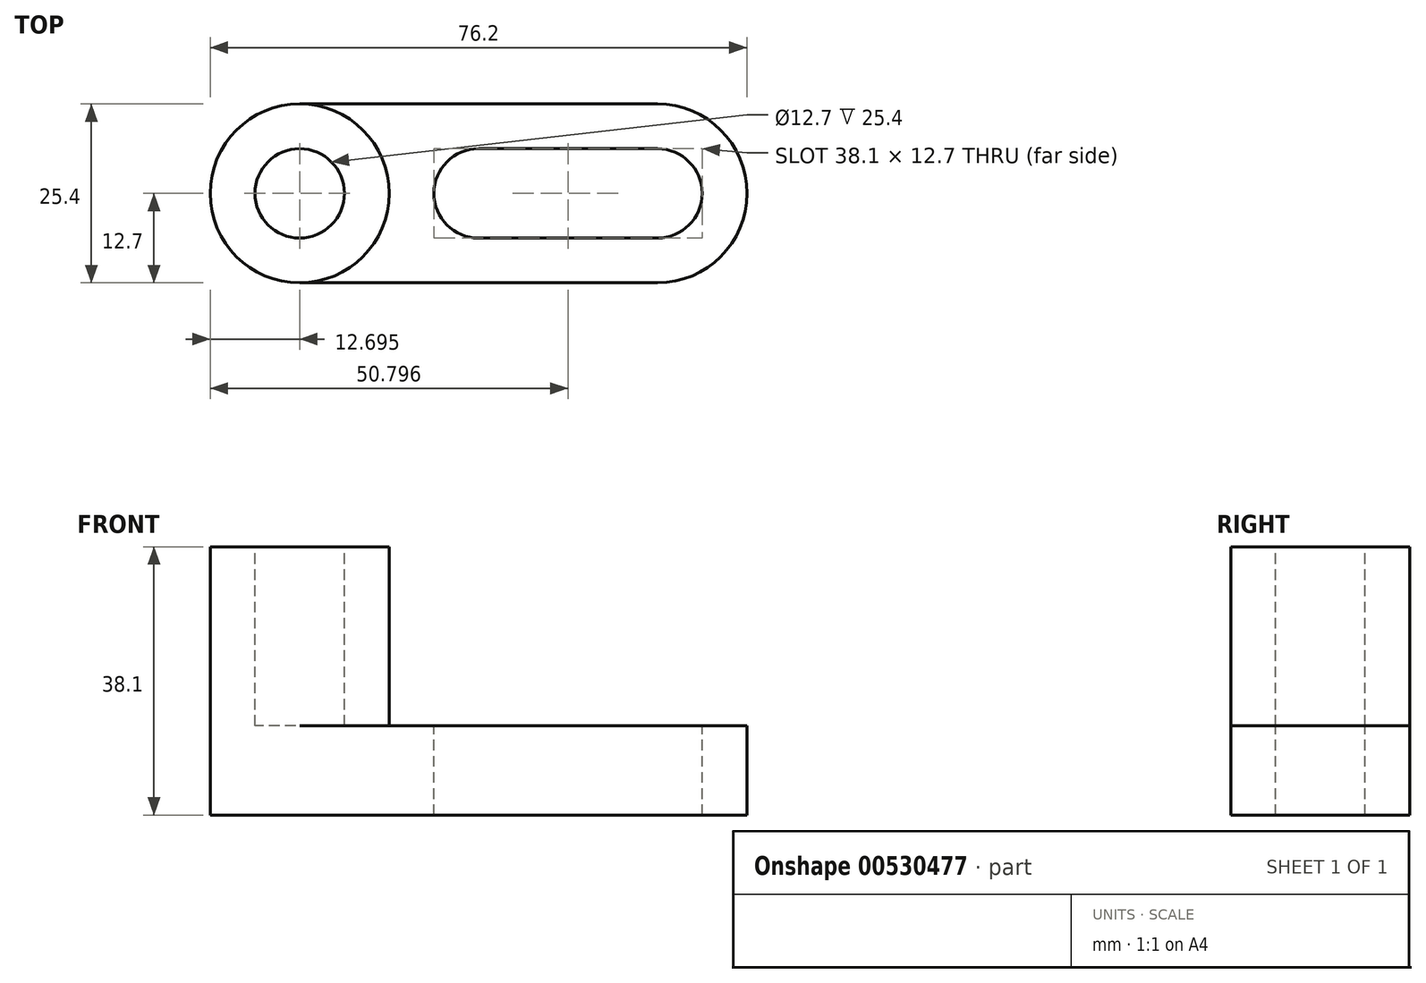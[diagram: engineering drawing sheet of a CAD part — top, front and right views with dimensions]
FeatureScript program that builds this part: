
annotation { "Feature Type Name" : "Feature", "Feature Type Description" : "" }
export const myFeature = defineFeature(function(context is Context, id is Id, definition is map)
    precondition{}
    {
        {
            var Q0;
            Q0=qCreatedBy(makeId("Front.planeOp"),FACE);
            var sketch = newSketch(context, id + "F0", { "sketchPlane" : qUnion([Q0])});
            skLineSegment(sketch, "E0", {"start": v(-91.03, 0) * mm, "end": v(-14.83, 0) * mm});
            skLineSegment(sketch, "E1", {"start": v(-14.83, 0) * mm, "end": v(-14.83, 12.7) * mm});
            skLineSegment(sketch, "E2", {"start": v(-14.83, 12.7) * mm, "end": v(-65.63, 12.7) * mm});
            skLineSegment(sketch, "E3", {"start": v(-65.63, 12.7) * mm, "end": v(-65.63, 38.1) * mm});
            skLineSegment(sketch, "E4", {"start": v(-65.63, 38.1) * mm, "end": v(-91.03, 38.1) * mm});
            skLineSegment(sketch, "E5", {"start": v(-91.03, 38.1) * mm, "end": v(-91.03, 0) * mm});
            skSolve(sketch);
        }
        {
            var Q0;
            Q0=makeQuery(id+"F0.imprint","IMPRINT",FACE,{"disambiguationData":[TD([[makeQuery(id+"F0.imprint","IMPRINT",EDGE,{"derivedFrom":sQuery(id+"F0.wireOp",EDGE,"E0")}),1.0]])]});
            extrude(context, id + "F1", {"entities" : qUnion([Q0]), "depth" : 25.4 * mm, "offsetDistance" : 25.4 * mm});
        }
        {
            var Q0;
            Q0=makeQuery(id+"F1.opExtrude","SWEPT_FACE",FACE,{"disambiguationData":[OSD([sQuery(id+"F0.wireOp",EDGE,"E4")])]});
            var sketch = newSketch(context, id + "F2", { "sketchPlane" : qUnion([Q0])});
            skCircle(sketch, "E6", {"center": v(-78.33, -12.7) * mm, "radius": 12.7 * mm});
            skPoint(sketch, "E6.centerSnap0", {"position": v(-65.63, -12.7) * mm});
            skCircle(sketch, "E7", {"center": v(-78.33, -12.7) * mm, "radius": 6.35 * mm});
            skSolve(sketch);
        }
        {
            var Q0;
            {var subQ0=sQuery(id+"F2.wireOp",EDGE,"E6");var subQ1=sQuery(id+"F0.wireOp",EDGE,"E4");var subQ2=makeQuery(id+"F1.opExtrude","CAP_EDGE",EDGE,{"disambiguationData":[OSD([subQ1])],"isStart":true});var subQ3=makeQuery(id+"F2.imprint","INTERSECT",VERTEX,{"derivedFrom":[subQ2,subQ0]});Q0=makeQuery(id+"F2.imprint","IMPRINT",FACE,{"disambiguationData":[TD([[makeQuery(id+"F2.imprint","IMPRINT",EDGE,{"disambiguationData":[TD([[subQ3,1.0]])],"derivedFrom":subQ0}),-1.0]])]});}
            var Q1;
            Q1=makeQuery(id+"F2.imprint","IMPRINT",FACE,{"disambiguationData":[TD([[makeQuery(id+"F2.imprint","IMPRINT",EDGE,{"derivedFrom":sQuery(id+"F2.wireOp",EDGE,"E7")}),1.0]])]});
            var Q2;
            {var subQ0=sQuery(id+"F2.wireOp",EDGE,"E6");var subQ1=sQuery(id+"F0.wireOp",EDGE,"E4");var subQ4=makeQuery(id+"F1.opExtrude","CAP_EDGE",EDGE,{"disambiguationData":[OSD([subQ1])],"isStart":false});var subQ5=makeQuery(id+"F2.imprint","INTERSECT",VERTEX,{"derivedFrom":[subQ4,subQ0]});Q2=makeQuery(id+"F2.imprint","IMPRINT",FACE,{"disambiguationData":[TD([[makeQuery(id+"F2.imprint","IMPRINT",EDGE,{"disambiguationData":[TD([[subQ5,-1.0]])],"derivedFrom":subQ0}),-1.0]])]});}
            var Q3;
            {var subQ0=sQuery(id+"F2.wireOp",EDGE,"E6");var subQ1=sQuery(id+"F0.wireOp",EDGE,"E4");var subQ4=makeQuery(id+"F1.opExtrude","CAP_EDGE",EDGE,{"disambiguationData":[OSD([subQ1])],"isStart":false});var subQ5=makeQuery(id+"F2.imprint","INTERSECT",VERTEX,{"derivedFrom":[subQ4,subQ0]});Q3=makeQuery(id+"F2.imprint","IMPRINT",FACE,{"disambiguationData":[TD([[makeQuery(id+"F2.imprint","IMPRINT",EDGE,{"disambiguationData":[TD([[subQ5,1.0]])],"derivedFrom":subQ0}),-1.0]])]});}
            var Q4;
            {var subQ0=sQuery(id+"F2.wireOp",EDGE,"E6");var subQ1=sQuery(id+"F0.wireOp",EDGE,"E4");var subQ2=makeQuery(id+"F1.opExtrude","CAP_EDGE",EDGE,{"disambiguationData":[OSD([subQ1])],"isStart":true});var subQ3=makeQuery(id+"F2.imprint","INTERSECT",VERTEX,{"derivedFrom":[subQ2,subQ0]});Q4=makeQuery(id+"F2.imprint","IMPRINT",FACE,{"disambiguationData":[TD([[makeQuery(id+"F2.imprint","IMPRINT",EDGE,{"disambiguationData":[TD([[subQ3,-1.0]])],"derivedFrom":subQ0}),-1.0]])]});}
            extrude(context, id + "F3", {"entities" : qUnion([Q0, Q1, Q2, Q3, Q4]), "operationType" : NewBodyOperationType.REMOVE, "oppositeDirection" : true, "depth" : 25.4 * mm, "offsetDistance" : 25.4 * mm});
        }
        {
            var Q0;
            {var subQ0=sQuery(id+"F0.wireOp",EDGE,"E4");var subQ1=makeQuery(id+"F1.opExtrude","CAP_EDGE",EDGE,{"disambiguationData":[OSD([subQ0])],"isStart":true});var subQ2=sQuery(id+"F0.wireOp",EDGE,"E5");var subQ3=makeQuery(id+"F1.opExtrude","SWEPT_EDGE",EDGE,{"disambiguationData":[OSD([subQ0,subQ2])]});var subQ4=makeQuery(id+"F2.imprint","INTERSECT",VERTEX,{"derivedFrom":[subQ3,subQ1]});var subQ5=sQuery(id+"F2.wireOp",EDGE,"E6");var subQ6=makeQuery(id+"F2.imprint","INTERSECT",VERTEX,{"derivedFrom":[subQ1,subQ5]});Q0=makeQuery(id+"F3.boolean.opBoolean","COPY",FACE,{"derivedFrom":makeQuery(id+"F3.opExtrude","CAP_FACE",FACE,{"disambiguationData":[OSD([subQ0,subQ2,subQ5]),TDD([makeQuery(id+"F2.imprint","IMPRINT",EDGE,{"disambiguationData":[TD([[subQ6,-1.0]])],"derivedFrom":subQ5}),makeQuery(id+"F2.imprint","IMPRINT",EDGE,{"disambiguationData":[TD([[subQ4,1.0]])],"derivedFrom":subQ3}),makeQuery(id+"F2.imprint","IMPRINT",EDGE,{"disambiguationData":[TD([[subQ6,-1.0]])],"derivedFrom":subQ1})])],"isStart":false})});}
            var Q1;
            {var subQ0=sQuery(id+"F0.wireOp",EDGE,"E4");var subQ1=makeQuery(id+"F1.opExtrude","CAP_EDGE",EDGE,{"disambiguationData":[OSD([subQ0])],"isStart":false});var subQ2=sQuery(id+"F0.wireOp",EDGE,"E5");var subQ3=makeQuery(id+"F1.opExtrude","SWEPT_EDGE",EDGE,{"disambiguationData":[OSD([subQ0,subQ2])]});var subQ4=makeQuery(id+"F2.imprint","INTERSECT",VERTEX,{"derivedFrom":[subQ3,subQ1]});var subQ5=sQuery(id+"F2.wireOp",EDGE,"E6");var subQ6=makeQuery(id+"F2.imprint","INTERSECT",VERTEX,{"derivedFrom":[subQ1,subQ5]});Q1=makeQuery(id+"F3.boolean.opBoolean","COPY",FACE,{"derivedFrom":makeQuery(id+"F3.opExtrude","CAP_FACE",FACE,{"disambiguationData":[OSD([subQ0,subQ2,subQ5]),TDD([makeQuery(id+"F2.imprint","IMPRINT",EDGE,{"disambiguationData":[TD([[subQ6,1.0]])],"derivedFrom":subQ5}),makeQuery(id+"F2.imprint","IMPRINT",EDGE,{"disambiguationData":[TD([[subQ4,-1.0]])],"derivedFrom":subQ3}),makeQuery(id+"F2.imprint","IMPRINT",EDGE,{"disambiguationData":[TD([[subQ6,-1.0]])],"derivedFrom":subQ1})])],"isStart":false})});}
            extrude(context, id + "F4", {"entities" : qUnion([Q0, Q1]), "operationType" : NewBodyOperationType.REMOVE, "oppositeDirection" : true, "depth" : 25.4 * mm, "offsetDistance" : 25.4 * mm});
        }
        {
            var Q0;
            {var subQ0=sQuery(id+"F0.wireOp",EDGE,"E4");var subQ1=makeQuery(id+"F1.opExtrude","CAP_EDGE",EDGE,{"disambiguationData":[OSD([subQ0])],"isStart":false});var subQ2=sQuery(id+"F0.wireOp",EDGE,"E3");var subQ3=makeQuery(id+"F1.opExtrude","SWEPT_EDGE",EDGE,{"disambiguationData":[OSD([subQ2,subQ0])]});var subQ4=makeQuery(id+"F2.imprint","INTERSECT",VERTEX,{"derivedFrom":[subQ3,subQ1]});var subQ5=sQuery(id+"F2.wireOp",EDGE,"E6");var subQ6=makeQuery(id+"F2.imprint","INTERSECT",VERTEX,{"derivedFrom":[subQ1,subQ5]});var subQ8=makeQuery(id+"F1.opExtrude","CAP_EDGE",EDGE,{"disambiguationData":[OSD([subQ0])],"isStart":true});var subQ9=makeQuery(id+"F2.imprint","INTERSECT",VERTEX,{"derivedFrom":[subQ3,subQ8]});var subQ10=makeQuery(id+"F2.imprint","INTERSECT",VERTEX,{"derivedFrom":[subQ8,subQ5]});Q0=makeQuery(id+"F3.boolean.opBoolean","MERGE",FACE,{"derivedFrom":[makeQuery(id+"F1.opExtrude","SWEPT_FACE",FACE,{"disambiguationData":[OSD([sQuery(id+"F0.wireOp",EDGE,"E2")])]}),makeQuery(id+"F3.opExtrude","CAP_FACE",FACE,{"disambiguationData":[OSD([subQ2,subQ0,subQ5]),TDD([makeQuery(id+"F2.imprint","IMPRINT",EDGE,{"disambiguationData":[TD([[subQ10,1.0]])],"derivedFrom":subQ5}),makeQuery(id+"F2.imprint","IMPRINT",EDGE,{"disambiguationData":[TD([[subQ9,1.0]])],"derivedFrom":subQ3}),makeQuery(id+"F2.imprint","IMPRINT",EDGE,{"disambiguationData":[TD([[subQ10,1.0]])],"derivedFrom":subQ8})])],"isStart":false}),makeQuery(id+"F3.opExtrude","CAP_FACE",FACE,{"disambiguationData":[OSD([subQ2,subQ0,subQ5]),TDD([makeQuery(id+"F2.imprint","IMPRINT",EDGE,{"disambiguationData":[TD([[subQ6,-1.0]])],"derivedFrom":subQ5}),makeQuery(id+"F2.imprint","IMPRINT",EDGE,{"disambiguationData":[TD([[subQ4,-1.0]])],"derivedFrom":subQ3}),makeQuery(id+"F2.imprint","IMPRINT",EDGE,{"disambiguationData":[TD([[subQ6,1.0]])],"derivedFrom":subQ1})])],"isStart":false})]});}
            var sketch = newSketch(context, id + "F5", { "sketchPlane" : qUnion([Q0])});
            skCircle(sketch, "E8", {"center": v(-52.93, -12.7) * mm, "radius": 6.35 * mm});
            skPoint(sketch, "E8.centerSnap0", {"position": v(-65.63, -12.7) * mm});
            skCircle(sketch, "E9", {"center": v(-27.53, -12.7) * mm, "radius": 6.35 * mm});
            skLineSegment(sketch, "E10", {"start": v(-52.93, -6.35) * mm, "end": v(-27.53, -6.35) * mm});
            skLineSegment(sketch, "E11", {"start": v(-52.93, -19.05) * mm, "end": v(-27.53, -19.05) * mm});
            skArc(sketch, "E12", {"start": v(-27.53, -25.4) * mm, "mid": v(-14.83, -12.7) * mm, "end": v(-27.53, 0) * mm});
            skSolve(sketch);
        }
        {
            var Q0;
            Q0 = qSketchRegion(id + "F5", true);
            var Q1;
            {var subQ0=sQuery(id+"F5.wireOp",EDGE,"E12");var subQ3=sQuery(id+"F0.wireOp",EDGE,"E2");var subQ6=makeQuery(id+"F1.opExtrude","SWEPT_EDGE",EDGE,{"disambiguationData":[OSD([sQuery(id+"F0.wireOp",EDGE,"E1"),subQ3])]});var subQ7=makeQuery(id+"F5.imprint","INTERSECT",VERTEX,{"derivedFrom":[subQ6,subQ0]});Q1=makeQuery(id+"F5.imprint","IMPRINT",FACE,{"disambiguationData":[TD([[makeQuery(id+"F5.imprint","IMPRINT",EDGE,{"disambiguationData":[TD([[subQ7,1.0]])],"derivedFrom":subQ0}),-1.0]])]});}
            var Q2;
            {var subQ0=sQuery(id+"F5.wireOp",EDGE,"E12");var subQ3=sQuery(id+"F0.wireOp",EDGE,"E2");var subQ6=makeQuery(id+"F1.opExtrude","SWEPT_EDGE",EDGE,{"disambiguationData":[OSD([sQuery(id+"F0.wireOp",EDGE,"E1"),subQ3])]});var subQ7=makeQuery(id+"F5.imprint","INTERSECT",VERTEX,{"derivedFrom":[subQ6,subQ0]});Q2=makeQuery(id+"F5.imprint","IMPRINT",FACE,{"disambiguationData":[TD([[makeQuery(id+"F5.imprint","IMPRINT",EDGE,{"disambiguationData":[TD([[subQ7,-1.0]])],"derivedFrom":subQ0}),-1.0]])]});}
            extrude(context, id + "F6", {"entities" : qUnion([Q0, Q1, Q2]), "operationType" : NewBodyOperationType.REMOVE, "oppositeDirection" : true, "depth" : 25.4 * mm, "offsetDistance" : 25.4 * mm});
        }
    });
